annotation { "Feature Type Name" : "Feature", "Feature Type Description" : "" }
export const myFeature = defineFeature(function(context is Context, id is Id, definition is map)
    precondition{}
    {
        {
            var Q0;
            Q0=qCreatedBy(makeId("Right.planeOp"),FACE);
            var sketch = newSketch(context, id + "F0", { "sketchPlane" : qUnion([Q0])});
            skLineSegment(sketch, "E0.bottom", {"start": v(-0.23, 0.08) * mm, "end": v(0.23, 0.08) * mm, "construction": true});
            skLineSegment(sketch, "E0.top", {"start": v(-0.23, 0) * mm, "end": v(0.23, 0) * mm});
            skLineSegment(sketch, "E0.left", {"start": v(-0.23, 0.08) * mm, "end": v(-0.23, 0) * mm, "construction": true});
            skLineSegment(sketch, "E0.right", {"start": v(0.23, 0.08) * mm, "end": v(0.23, 0) * mm, "construction": true});
            skArc(sketch, "E1", {"start": v(0.23, 0) * mm, "mid": v(0, 0.12) * mm, "end": v(-0.23, 0) * mm});
            skLineSegment(sketch, "E2", {"start": v(0, -0.16) * mm, "end": v(0, 0.32) * mm, "construction": true});
            skLineSegment(sketch, "E3", {"start": v(-0.08, 0.1) * mm, "end": v(-0.06, 0.32) * mm});
            skLineSegment(sketch, "E4", {"start": v(-0.06, 0.32) * mm, "end": v(0, 0.32) * mm});
            skLineSegment(sketch, "E5.MirrorCS", {"start": v(0.06, 0.32) * mm, "end": v(0, 0.32) * mm});
            skLineSegment(sketch, "E6.MirrorCS", {"start": v(0.08, 0.1) * mm, "end": v(0.06, 0.32) * mm});
            skSolve(sketch);
        }
        {
            var Q0;
            {var subQ0=sQuery(id+"F0.wireOp",EDGE,"E0.top");Q0=makeQuery(id+"F0.imprint","IMPRINT",FACE,{"disambiguationData":[TD([[makeQuery(id+"F0.imprint","IMPRINT",EDGE,{"derivedFrom":subQ0}),1.0]])]});}
            var Q1;
            {var subQ0=sQuery(id+"F0.wireOp",EDGE,"E3");Q1=makeQuery(id+"F0.imprint","IMPRINT",FACE,{"disambiguationData":[TD([[makeQuery(id+"F0.imprint","IMPRINT",EDGE,{"derivedFrom":subQ0}),-1.0]])]});}
            extrude(context, id + "F1", {"entities" : qUnion([Q0, Q1]), "depth" : 0.15 * mm, "symmetric" : true});
        }
        {
            var Q0;
            Q0=qCreatedBy(makeId("Right.planeOp"),FACE);
            var sketch = newSketch(context, id + "F2", { "sketchPlane" : qUnion([Q0])});
            skArc(sketch, "E7.0", {"start": v(0.23, 0) * mm, "mid": v(0, 0.12) * mm, "end": v(-0.23, 0) * mm});
            skLineSegment(sketch, "E8.0", {"start": v(-0.23, 0) * mm, "end": v(0.23, 0) * mm});
            skLineSegment(sketch, "E9", {"start": v(0, -0.16) * mm, "end": v(-0.25, 0.25) * mm, "construction": true});
            skLineSegment(sketch, "E10", {"start": v(-0.2, 0.03) * mm, "end": v(-0.3, 0.22) * mm});
            skLineSegment(sketch, "E11", {"start": v(-0.3, 0.22) * mm, "end": v(-0.25, 0.25) * mm});
            skLineSegment(sketch, "E12.MirrorCS", {"start": v(-0.2, 0.28) * mm, "end": v(-0.25, 0.25) * mm});
            skLineSegment(sketch, "E13.MirrorCS", {"start": v(-0.08, 0.1) * mm, "end": v(-0.2, 0.28) * mm});
            skSolve(sketch);
        }
        {
            var Q0;
            {var subQ0=sQuery(id+"F2.wireOp",EDGE,"E10");Q0=makeQuery(id+"F2.imprint","IMPRINT",FACE,{"disambiguationData":[TD([[makeQuery(id+"F2.imprint","IMPRINT",EDGE,{"derivedFrom":subQ0}),-1.0]])]});}
            var Q1;
            {var subQ0=sQuery(id+"F2.wireOp",EDGE,"E8.0");Q1=makeQuery(id+"F2.imprint","IMPRINT",FACE,{"disambiguationData":[TD([[makeQuery(id+"F2.imprint","IMPRINT",EDGE,{"derivedFrom":subQ0}),1.0]])]});}
            extrude(context, id + "F3", {"entities" : qUnion([Q0, Q1]), "depth" : 0.15 * mm, "symmetric" : true});
        }
        {
            var Q0;
            Q0=makeQuery(id+"F3.opExtrude","SWEPT_BODY",BODY,{"disambiguationData":[OSD([sQuery(id+"F2.wireOp",EDGE,"E7.0"),sQuery(id+"F2.wireOp",EDGE,"E8.0"),sQuery(id+"F2.wireOp",EDGE,"E10"),sQuery(id+"F2.wireOp",EDGE,"E11"),sQuery(id+"F2.wireOp",EDGE,"E12.MirrorCS"),sQuery(id+"F2.wireOp",EDGE,"E13.MirrorCS")])]});
            transform(context, id + "F4", {"entities" : qUnion([Q0]), "transformType" : TransformType.COPY});
        }
    });